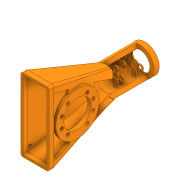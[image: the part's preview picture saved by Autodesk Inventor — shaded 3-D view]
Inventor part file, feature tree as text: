
AUTODESK INVENTOR PART (.ipt)
format: ipt  version: 2020 (Build 240168000, 168)  size: 1,159,680 bytes
history: native  units: in
note: dims shown in document units (in); Inventor stores cm internally (conversion verified against a paired STEP export)
features: chamfer x23, sketch x22, extrude x19, projected_geometry x11, plane x3, loft x2, fillet x1, other x1
ambient origin geometry x8: Origin, YZ Plane, XZ Plane, XY Plane, X Axis, Y Axis, Z Axis, Center Point
bodies: Solid1 (feature_tree)
feature tree (82):
  extrude  "Extrusion1"  Depth=2.0472in
  extrude  "Extrusion2"  Depth=1.6535in
  chamfer  "Chamfer1"  Distance=0.5512in
  extrude  "Extrusion3"  Depth=0.0157in
  extrude  "Extrusion4"  Depth=0.2756in TaperAngle=0.0deg
  extrude  "Extrusion5"  Depth=0.315in
  extrude  "Extrusion6"  Depth=0.4724in
  extrude  "Extrusion7"  Depth=0.0787in
  plane  "Work Plane1"
  extrude  "Extrusion8"  Depth=0.1575in
  plane  "Work Plane2"
  extrude  "Extrusion9"  Depth=1.0994in
  sketch  "Sketch11"  dims[d31=15.0deg d32=0.4921in d33=0.0in]
  plane  "Work Plane3"
  extrude  "Extrusion10"  Depth=0.4921in TaperAngle=0.0deg
  extrude  "Extrusion11"  Depth=1.5748in TaperAngle=360.0deg
  loft  "Loft1"
  loft  "Loft2"
  sketch  "Sketch16"  dims[d47=0.315in d48=0.4331in]
  extrude  "Extrusion12"  Depth=0.0984in TaperAngle=0.0deg
  extrude  "Extrusion13"  Depth=0.4331in
  extrude  "Extrusion14"  Depth=0.6161in
  extrude  "Extrusion15"  Depth=0.1575in
  chamfer  "Chamfer2"  Distance=0.0984in
  chamfer  "Chamfer3"  [1 undecoded]
  chamfer  "Chamfer4"  Distance=1.6654in
  chamfer  "Chamfer5"  Distance=1.6654in
  chamfer  "Chamfer6"  Distance=0.1969in
  chamfer  "Chamfer7"  Distance=0.1969in
  chamfer  "Chamfer8"  Distance=0.3484in
  chamfer  "Chamfer9"  Distance=0.3484in
  chamfer  "Chamfer10"  Distance=0.1969in
  chamfer  "Chamfer11"  Distance=0.1969in
  chamfer  "Chamfer12"  Distance=0.1969in
  chamfer  "Chamfer13"  Distance=0.3937in
  chamfer  "Chamfer14"  Distance=0.7874in
  chamfer  "Chamfer15"  Angle=90.0deg  [1 undecoded]
  chamfer  "Chamfer16"  Angle=90.0deg  [1 undecoded]
  chamfer  "Chamfer17"  Angle=90.0deg  [1 undecoded]
  chamfer  "Chamfer18"  Angle=90.0deg  [1 undecoded]
  chamfer  "Chamfer19"  Distance=0.7874in
  chamfer  "Chamfer20"  Distance=0.3937in
  chamfer  "Chamfer21"  Distance=0.3937in
  chamfer  "Chamfer22"  Distance=0.7874in
  fillet  "Fillet1"  Radius=0.1969in
  chamfer  "Chamfer23"  Distance=0.8858in
  extrude  "Extrusion19"  Depth=0.1969in
  extrude  "Extrusion20"  Depth=0.1969in
  extrude  "Extrusion21"  TaperAngle=0.0deg  [1 undecoded]
  extrude  "Extrusion22"  TaperAngle=0.0deg  [1 undecoded]
  sketch  "Sketch1"  dims[d0=2.3622in d1=2.0472in]
  sketch  "Sketch2"  dims[d2=0.2756in d3=0.0in d4=1.6535in d5=0.5512in d6=0.0in]
  sketch  "Sketch3"  dims[d7=0.2756in d8=0.125in d9=0.0137in d10=0.0157in]
  sketch  "Sketch5"  dims[d11=4.7244in d13=360.0deg d15=0.2756in d16=0.0in]
  sketch  "Sketch6"  dims[d17=0.5512in d19=0.315in]
  projected_geometry  "Projected Loop1"
  sketch  "Sketch7"  dims[d20=0.315in d21=0.4724in]
  projected_geometry  "Projected Loop2"
  sketch  "Sketch8"  dims[d22=0.4724in d23=0.0787in d24=0.0787in d25=0.0787in]
  projected_geometry  "Projected Loop3"
  sketch  "Sketch9"  dims[d26=0.0984in d27=0.0in d28=0.1575in]
  sketch  "Sketch10"  dims[d29=0.1575in d30=1.0994in]
  sketch  "Sketch12"  dims[d34=1.4567in d35=0.0in d36=1.5748in d38=360.0deg]
  sketch  "Sketch13"  dims[d40=0.0787in d41=0.0787in]
  projected_geometry  "Projected Loop4"
  other  "Edges1"
  sketch  "Sketch14"  dims[d42=0.0787in d43=0.0787in]
  projected_geometry  "Projected Loop5"
  sketch  "Sketch15"  dims[d44=0.0787in d45=0.0984in d46=0.0in]
  projected_geometry  "Projected Loop6"
  projected_geometry  "Projected Loop7"
  sketch  "Sketch19"  dims[d49=0.0984in d50=0.0in d51=0.6161in]
  projected_geometry  "Projected Loop8"
  sketch  "Sketch20"  dims[d52=0.1575in d53=0.1575in d54=0.0984in d55=0.0in]
  projected_geometry  "Projected Loop9"
  sketch  "Sketch21"  dims[d56=6.6929in]
  sketch  "Sketch25"  dims[d57=0.8858in]
  sketch  "Sketch26"  dims[d58=1.6654in]
  projected_geometry  "Projected Loop11"
  sketch  "Sketch27"  dims[d59=1.6654in]
  projected_geometry  "Projected Loop12"
  sketch  "Sketch28"  dims[d60=0.0in d61=0.0in d62=1.6654in d63=1.6654in d64=0.1969in d65=0.1969in d66=0.3484in d67=0.3484in d68=0.1969in d69=0.1969in d70=0.1969in d71=0.3937in d72=0.0in d73=0.7874in d74=0.0in d75=0.0in d76=90.0deg d77=0.0in d78=90.0deg d79=0.0in d80=90.0deg d81=0.0in d82=90.0deg d86=0.7874in d87=0.0in d90=0.3937in d91=0.3937in d92=0.7874in d93=0.0in d94=0.1969in d95=0.0in d96=0.8858in d97=1.6654in d98=1.6654in d99=0.0in d100=0.0in d101=0.2224in d102=0.1575in d103=0.1575in d104=0.1575in d105=0.1575in d106=0.0984in d107=0.0984in d108=0.1969in d109=0.0in d122=0.1575in d123=0.0787in d124=45.0deg d125=0.0787in d126=0.1575in d127=45.0deg d128=0.1575in d129=0.0787in d130=45.0deg d131=0.0787in d132=0.1575in d133=45.0deg d134=0.1575in d135=0.0787in d136=45.0deg d137=0.1575in d138=0.0787in d139=45.0deg d140=0.1575in d141=0.0787in d142=45.0deg d143=0.1575in d144=0.0787in d145=45.0deg d146=0.0787in d147=0.1575in d148=45.0deg d149=0.1575in d150=0.0787in d151=45.0deg d152=0.1575in d153=0.0787in d154=45.0deg d155=0.0787in d156=0.1575in d157=45.0deg d158=0.0591in d159=0.1575in d160=0.0137in d161=0.0591in d162=0.1575in d163=0.0137in d164=0.0591in d165=0.1575in d166=0.0137in d167=0.0591in d168=0.1575in d169=0.0137in d170=0.0591in d171=0.1575in d172=0.0137in d173=0.0591in d174=0.1575in d175=0.0137in d176=0.0591in d177=0.1575in d178=0.0137in d179=0.0591in d180=0.1575in d181=0.0137in d182=0.0591in d183=0.1575in d184=0.0137in d185=0.0197in d193=0.0984in d194=0.3937in d195=0.125in d196=45.0deg d197=0.2756in d198=0.1969in d199=0.0in d200=0.2756in d201=2.7559in d202=0.2756in d203=0.2756in d204=0.2756in d205=0.2756in d206=0.2756in d207=0.2756in d208=0.2756in d209=0.0394in d210=0.2047in d211=0.0in d212=0.1969in d213=0.2756in d214=0.0in d215=1.0in d216=0.0in]
note: 7 required parameter values undecoded (feature->parameter linkage not recoverable at this tier; creation-order binding heuristic only, values carry confidence <= 0.55)
